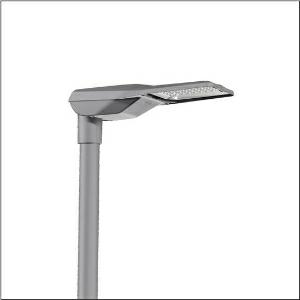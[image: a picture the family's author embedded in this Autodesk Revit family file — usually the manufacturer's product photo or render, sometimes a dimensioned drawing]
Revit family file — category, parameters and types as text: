
# Revit family: streetlight_sl_21_iq_mini___st0_8a_5xe2c41g08hb_fab9
name_source: partatom
category: Lighting Fixtures
units: mm (PartAtom-declared; Revit-internal decimal feet)

## family parameters
Cut with Voids When Loaded = No
Host = Face
Light Source = No
Part Type = Normal
Room Calculation Point = No
Round Connector Dimension = Use Diameter
Shared = No

## types (1)
- --- (1 x LED, 9860 lm, 70.9 W, 4000K)
    Apparent Load = 71 VA
    CIE Flux Codes = 38 75 97 100 100
    Color Rendering = 70
    Color Temperature = 4000K
    Default Elevation = 1800 mm
    Description = Streetlight SL 21 iQ mini, mast luminaire, primary light control with lens, of PMMA, primary optical cover: cover, of toughened safety glass, transparent, light distribution: ST0.8a, light emission: direct distribution, primary light characteristic: asymmetric, installation type: post-top, side-entry, LED, High Power LED, rated luminous flux: 9.860lm, luminous efficacy: 139lm/W, light colour: 740, colour temperature: 4000K, control gear: iQ Street-Remote, control: Street-Remote, Auto-Match, Temp-Guard, Lumen-Switch, Night-Set, Smart-Wire, Light-Fading, Desk-Remote (wireless, voltage-free reading and setting of iQ features in the workshop via application-optimized NFC function/RFID function), optimised constant luminous flux control (CLO 2.0), pre-setting: linear dimming characteristic, mains connection: 220..240V, AC, 50/60Hz, start of lifetime: 71W, end of service life: 75W, reduction: 31W, luminaire housing, of diecast aluminium, powder-coated, Siteco® metallic grey (DB 702S), corrosivity category C5 mid according to DIN EN ISO 12944, please order mast flange separately, inclination adjustable: 0°, 5°, 10°, 15°, sealing non-destructively replaceable, multi-level sealing system, length: 628mm, width: 235mm, height: 110mm, mast flange for spigot size: 42mm (side-entry): 5XC10008XM4, 60/48mm (side-entry/post-top): 5XC10108XM2, 76/60mm (side-entry/post-top): 5XC10108XM1, mounting height: 4..8m, protection rating (complete): IP66, insulation class (complete): insulation class II (safety insulation), certification: CE, ENEC, ENEC+, VDE, impact resistance: IK10, permissible operating ambient temperature for outdoor applications: -40..+50°C, standard-compliant lighting for roads and squares, packaging unit: 1 piece

Light Distribution: ST0.8a
    Height = 110 mm
    Lamp = 1 x LED
    Lamp Light Flux = 9860 lm
    Lamp Power = 70.9 W
    Lamp count = 1
    Length = 625 mm
    Luminous efficacy = 139 lm/W
    Manufacturer = Siteco
    ModVariant = No
    Model = 5XE2C41G08HB
    Number of Poles = 1
    OnlyDefault = Yes
    Power Factor = 1
    Product Name = Streetlight SL 21 iQ mini | ST0.8a
    Product group = mast luminaire | pylon top
    ProductGroupID = 6100
    Protection Class = Protection class II
    Protection Degree = IP 66
    RLX_Detail_Level = 1
    RLX_Emergency_Light_Flux = 0 lm
    RLX_Emergency_Type = 0
    RLX_Emergency_Type_DB = No
    RlxData = <blob elided: 26349 chars, md5=dde42c6f>
    Socket = socket
    Standby Power = 0 W
    System Light Flux = 9860 lm
    System Power = 71 W
    Type Comments = factory setting: luminous flux: 100 % | dim-lin: 254 | 711 mA
    Type Image = l_1003519.jpg
    URL = http://relux.com
    VarID = @adj_157352
    Voltage = 0 V
    Weight = 0.00 kg
    Width = 234 mm

## geometry (parser evidence)
native form markers: Blend x4, Sweep x10
no freeform markers — native parametric forms only
